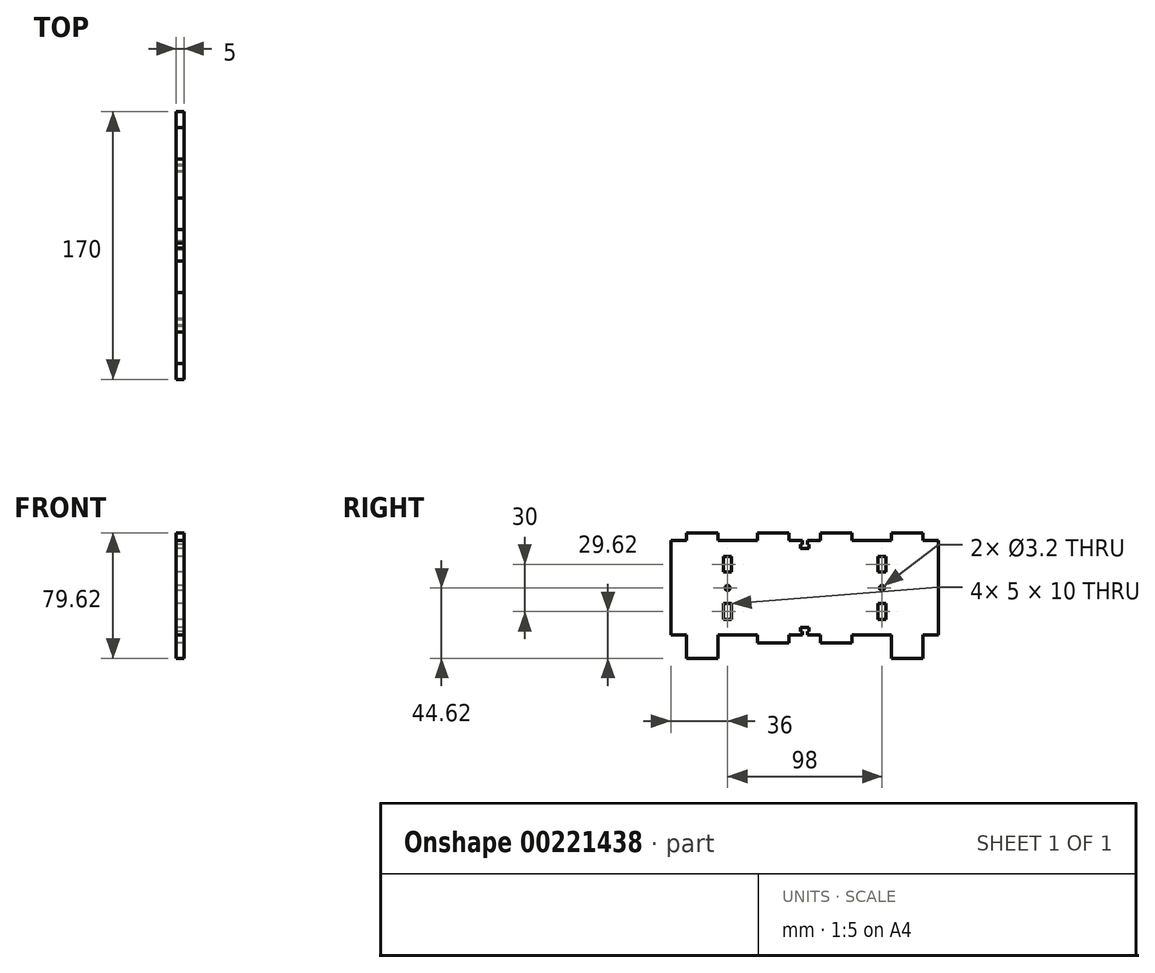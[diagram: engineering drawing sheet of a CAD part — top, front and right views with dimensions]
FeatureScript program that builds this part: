
annotation { "Feature Type Name" : "Feature", "Feature Type Description" : "" }
export const myFeature = defineFeature(function(context is Context, id is Id, definition is map)
    precondition{}
    {
        {
            assignVariable(context, id + "F0", {"name" : "thickness", "anyValue" : 5 * mm});
        }
        {
            var Q0;
            Q0=qCreatedBy(makeId("Right.planeOp"),FACE);
            var sketch = newSketch(context, id + "F1", { "sketchPlane" : qUnion([Q0])});
            skLineSegment(sketch, "E0.bottom", {"start": v(0, 0) * mm, "end": v(83.4, 0) * mm});
            skLineSegment(sketch, "E0.top", {"start": v(0, 60) * mm, "end": v(83.4, 60) * mm});
            skLineSegment(sketch, "E0.left", {"start": v(0, 0) * mm, "end": v(0, 60) * mm});
            skLineSegment(sketch, "E0.right", {"start": v(170, 0) * mm, "end": v(170, 60) * mm});
            skLineSegment(sketch, "E1", {"start": v(10, 0) * mm, "end": v(10, -14.62) * mm});
            skLineSegment(sketch, "E2", {"start": v(10, -14.62) * mm, "end": v(30, -14.62) * mm});
            skLineSegment(sketch, "E3", {"start": v(30, -14.62) * mm, "end": v(30, 0) * mm});
            skLineSegment(sketch, "E4", {"start": v(55, 0) * mm, "end": v(55, -5) * mm});
            skLineSegment(sketch, "E5", {"start": v(55, -5) * mm, "end": v(75, -5) * mm});
            skLineSegment(sketch, "E6", {"start": v(75, -5) * mm, "end": v(75, 0) * mm});
            skLineSegment(sketch, "E7", {"start": v(85, 60) * mm, "end": v(85, 0) * mm, "construction": true});
            skLineSegment(sketch, "E8.MirrorCS", {"start": v(95, -5) * mm, "end": v(95, 0) * mm});
            skLineSegment(sketch, "E9.MirrorCS", {"start": v(115, -5) * mm, "end": v(95, -5) * mm});
            skLineSegment(sketch, "E10.MirrorCS", {"start": v(115, 0) * mm, "end": v(115, -5) * mm});
            skLineSegment(sketch, "E11.MirrorCS", {"start": v(140, -14.62) * mm, "end": v(140, 0) * mm});
            skLineSegment(sketch, "E12.MirrorCS", {"start": v(160, -14.62) * mm, "end": v(140, -14.62) * mm});
            skLineSegment(sketch, "E13.MirrorCS", {"start": v(160, 0) * mm, "end": v(160, -14.62) * mm});
            skLineSegment(sketch, "E14", {"start": v(83.4, 0) * mm, "end": v(83.4, 2.5) * mm});
            skLineSegment(sketch, "E15", {"start": v(83.4, 2.5) * mm, "end": v(82.25, 2.5) * mm});
            skLineSegment(sketch, "E16", {"start": v(82.25, 2.5) * mm, "end": v(82.25, 5) * mm});
            skLineSegment(sketch, "E17", {"start": v(82.25, 5) * mm, "end": v(85, 5) * mm});
            skLineSegment(sketch, "E18.MirrorCS", {"start": v(86.6, 2.5) * mm, "end": v(87.75, 2.5) * mm});
            skLineSegment(sketch, "E19.MirrorCS", {"start": v(87.75, 5) * mm, "end": v(85, 5) * mm});
            skLineSegment(sketch, "E20.MirrorCS", {"start": v(87.75, 2.5) * mm, "end": v(87.75, 5) * mm});
            skLineSegment(sketch, "E21.MirrorCS", {"start": v(86.6, 0) * mm, "end": v(86.6, 2.5) * mm});
            skLineSegment(sketch, "E22", {"start": v(0, 30) * mm, "end": v(170, 30) * mm, "construction": true});
            skLineSegment(sketch, "E23.MirrorCS", {"start": v(83.4, 57.5) * mm, "end": v(82.25, 57.5) * mm});
            skLineSegment(sketch, "E24.MirrorCS", {"start": v(87.75, 57.5) * mm, "end": v(87.75, 55) * mm});
            skLineSegment(sketch, "E25.MirrorCS", {"start": v(86.6, 60) * mm, "end": v(86.6, 57.5) * mm});
            skLineSegment(sketch, "E26.MirrorCS", {"start": v(86.6, 57.5) * mm, "end": v(87.75, 57.5) * mm});
            skLineSegment(sketch, "E27.MirrorCS", {"start": v(82.25, 57.5) * mm, "end": v(82.25, 55) * mm});
            skLineSegment(sketch, "E28.MirrorCS", {"start": v(83.4, 60) * mm, "end": v(83.4, 57.5) * mm});
            skLineSegment(sketch, "E29.MirrorCS", {"start": v(82.25, 55) * mm, "end": v(85, 55) * mm});
            skLineSegment(sketch, "E30.MirrorCS", {"start": v(87.75, 55) * mm, "end": v(85, 55) * mm});
            skLineSegment(sketch, "E31.MirrorCS", {"start": v(95, 65) * mm, "end": v(95, 60) * mm});
            skLineSegment(sketch, "E32.MirrorCS", {"start": v(75, 65) * mm, "end": v(75, 60) * mm});
            skLineSegment(sketch, "E33.MirrorCS", {"start": v(55, 60) * mm, "end": v(55, 65) * mm});
            skLineSegment(sketch, "E34.MirrorCS", {"start": v(115, 60) * mm, "end": v(115, 65) * mm});
            skLineSegment(sketch, "E35.MirrorCS", {"start": v(115, 65) * mm, "end": v(95, 65) * mm});
            skLineSegment(sketch, "E36.MirrorCS", {"start": v(55, 65) * mm, "end": v(75, 65) * mm});
            skLineSegment(sketch, "E37", {"start": v(10, 60) * mm, "end": v(10, 65) * mm});
            skLineSegment(sketch, "E38", {"start": v(10, 65) * mm, "end": v(30, 65) * mm});
            skLineSegment(sketch, "E39", {"start": v(30, 65) * mm, "end": v(30, 60) * mm});
            skLineSegment(sketch, "E40.MirrorCS", {"start": v(140, 65) * mm, "end": v(140, 60) * mm});
            skLineSegment(sketch, "E41.MirrorCS", {"start": v(160, 60) * mm, "end": v(160, 65) * mm});
            skLineSegment(sketch, "E42.MirrorCS", {"start": v(160, 65) * mm, "end": v(140, 65) * mm});
            skLineSegment(sketch, "E43.trimOffspring", {"start": v(86.6, 0) * mm, "end": v(170, 0) * mm});
            skLineSegment(sketch, "E44.trimOffspring", {"start": v(86.6, 60) * mm, "end": v(170, 60) * mm});
            skLineSegment(sketch, "E45.bottom", {"start": v(33.5, 20) * mm, "end": v(38.5, 20) * mm});
            skLineSegment(sketch, "E45.top", {"start": v(33.5, 10) * mm, "end": v(38.5, 10) * mm});
            skLineSegment(sketch, "E45.left", {"start": v(33.5, 20) * mm, "end": v(33.5, 10) * mm});
            skLineSegment(sketch, "E45.right", {"start": v(38.5, 20) * mm, "end": v(38.5, 10) * mm});
            skCircle(sketch, "E46", {"center": v(36, 30) * mm, "radius": 1.6 * mm});
            skPoint(sketch, "E46.centerSnap0", {"position": v(36, 20) * mm});
            skLineSegment(sketch, "E47.MirrorCS", {"start": v(33.5, 40) * mm, "end": v(38.5, 40) * mm});
            skLineSegment(sketch, "E48.MirrorCS", {"start": v(38.5, 40) * mm, "end": v(38.5, 50) * mm});
            skLineSegment(sketch, "E49.MirrorCS", {"start": v(33.5, 50) * mm, "end": v(38.5, 50) * mm});
            skLineSegment(sketch, "E50.MirrorCS", {"start": v(33.5, 40) * mm, "end": v(33.5, 50) * mm});
            skCircle(sketch, "E51.MirrorC", {"center": v(134, 30) * mm, "radius": 1.6 * mm});
            skLineSegment(sketch, "E52.MirrorCS", {"start": v(136.5, 20) * mm, "end": v(131.5, 20) * mm});
            skLineSegment(sketch, "E53.MirrorCS", {"start": v(131.5, 20) * mm, "end": v(131.5, 10) * mm});
            skLineSegment(sketch, "E54.MirrorCS", {"start": v(136.5, 40) * mm, "end": v(131.5, 40) * mm});
            skLineSegment(sketch, "E55.MirrorCS", {"start": v(131.5, 40) * mm, "end": v(131.5, 50) * mm});
            skLineSegment(sketch, "E56.MirrorCS", {"start": v(136.5, 10) * mm, "end": v(131.5, 10) * mm});
            skLineSegment(sketch, "E57.MirrorCS", {"start": v(136.5, 40) * mm, "end": v(136.5, 50) * mm});
            skPoint(sketch, "E58.MirrorP", {"position": v(134, 20) * mm});
            skLineSegment(sketch, "E59.MirrorCS", {"start": v(136.5, 20) * mm, "end": v(136.5, 10) * mm});
            skLineSegment(sketch, "E60.MirrorCS", {"start": v(136.5, 50) * mm, "end": v(131.5, 50) * mm});
            skSolve(sketch);
        }
        {
            var Q0;
            Q0 = qSketchRegion(id + "F1", true);
            extrude(context, id + "F2", {"entities" : qUnion([Q0]), "depth" : getVariable(context, 'thickness')});
        }
    });
